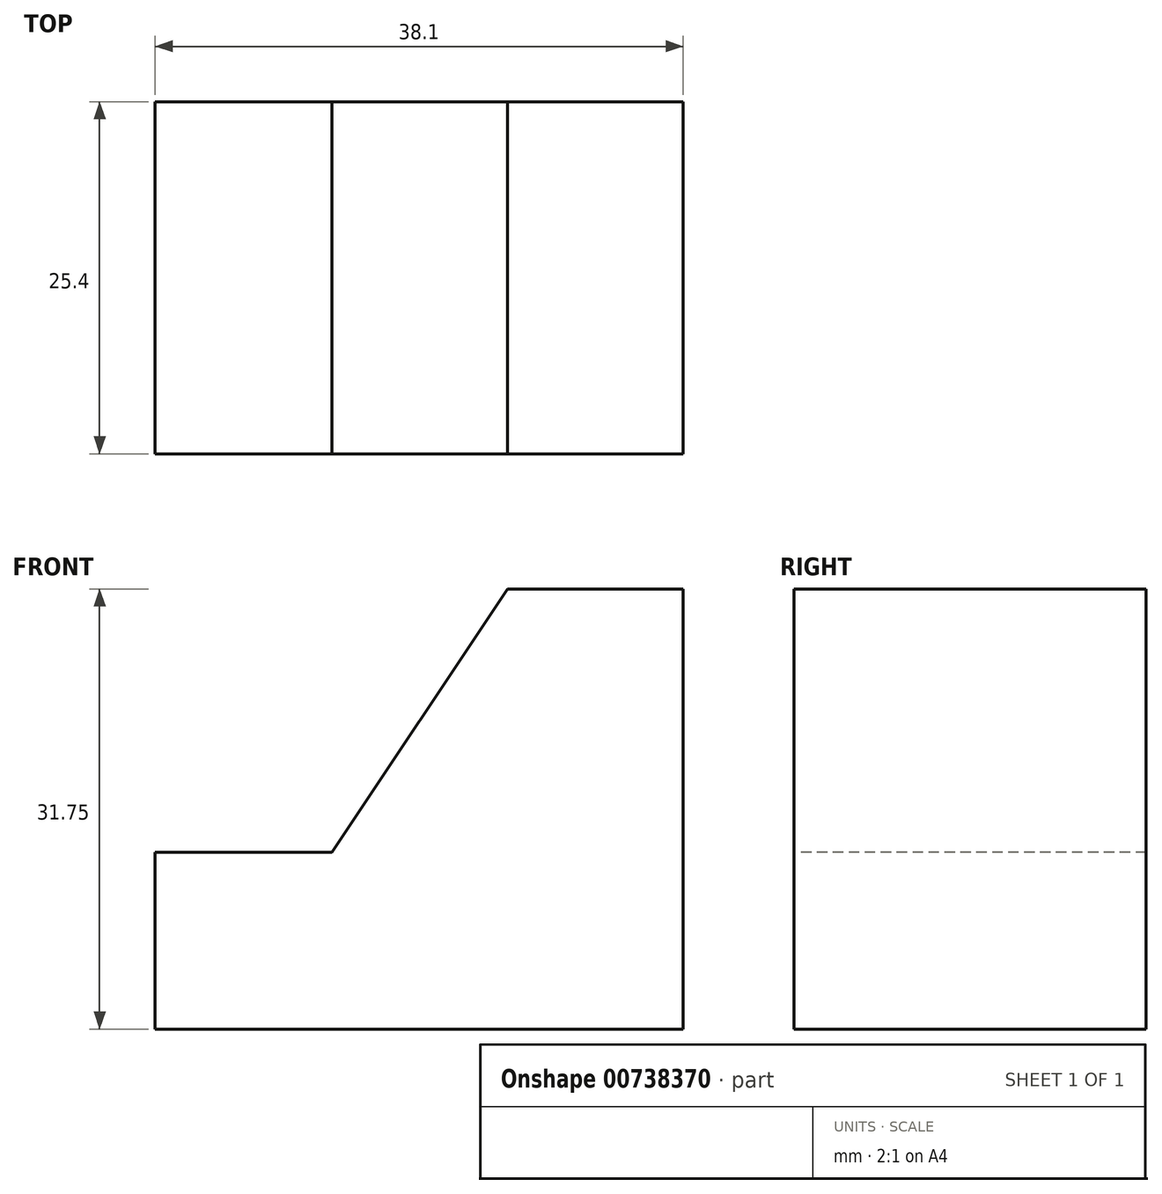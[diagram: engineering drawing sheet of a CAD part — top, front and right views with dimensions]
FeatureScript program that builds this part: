
annotation { "Feature Type Name" : "Feature", "Feature Type Description" : "" }
export const myFeature = defineFeature(function(context is Context, id is Id, definition is map)
    precondition{}
    {
        {
            var Q0;
            Q0=qCreatedBy(makeId("Front.planeOp"),FACE);
            var sketch = newSketch(context, id + "F0", { "sketchPlane" : qUnion([Q0])});
            skLineSegment(sketch, "E0", {"start": v(0, 0) * mm, "end": v(0, 31.75) * mm});
            skLineSegment(sketch, "E1", {"start": v(0, 31.75) * mm, "end": v(38.1, 31.75) * mm});
            skLineSegment(sketch, "E2", {"start": v(38.1, 31.75) * mm, "end": v(38.1, 0) * mm});
            skLineSegment(sketch, "E3", {"start": v(38.1, 0) * mm, "end": v(0, 0) * mm});
            skSolve(sketch);
        }
        {
            var Q0;
            Q0=makeQuery(id+"F0.imprint","IMPRINT",FACE,{"disambiguationData":[TD([[makeQuery(id+"F0.imprint","IMPRINT",EDGE,{"derivedFrom":sQuery(id+"F0.wireOp",EDGE,"E0")}),-1.0]])]});
            extrude(context, id + "F1", {"entities" : qUnion([Q0]), "depth" : 25.4 * mm, "offsetDistance" : 25.4 * mm});
        }
        {
            var Q0;
            Q0=qCreatedBy(makeId("Front.planeOp"),FACE);
            var sketch = newSketch(context, id + "F2", { "sketchPlane" : qUnion([Q0])});
            skLineSegment(sketch, "E4", {"start": v(23.02, 31.26) * mm, "end": v(23.02, 8.34) * mm});
            skLineSegment(sketch, "E5", {"start": v(23.02, 8.34) * mm, "end": v(0, 8.34) * mm});
            skLineSegment(sketch, "E6", {"start": v(0, 8.34) * mm, "end": v(0, 12.56) * mm});
            skLineSegment(sketch, "E7", {"start": v(0, 12.56) * mm, "end": v(23.02, 31.26) * mm});
            skSolve(sketch);
        }
        {
            var Q0;
            Q0=makeQuery(id+"F2.imprint","IMPRINT",FACE,{"disambiguationData":[TD([[makeQuery(id+"F2.imprint","IMPRINT",EDGE,{"derivedFrom":sQuery(id+"F2.wireOp",EDGE,"E4")}),-1.0]])]});
            extrude(context, id + "F3", {"entities" : qUnion([Q0]), "operationType" : NewBodyOperationType.REMOVE, "oppositeDirection" : true, "depth" : 25.4 * mm, "offsetDistance" : 25.4 * mm});
        }
        {
            var Q0;
            Q0=makeQuery(id+"F1.opExtrude","CAP_FACE",FACE,{"disambiguationData":[OSD([sQuery(id+"F0.wireOp",EDGE,"E0"),sQuery(id+"F0.wireOp",EDGE,"E1"),sQuery(id+"F0.wireOp",EDGE,"E2"),sQuery(id+"F0.wireOp",EDGE,"E3")])],"isStart":false});
            var sketch = newSketch(context, id + "F4", { "sketchPlane" : qUnion([Q0])});
            skLineSegment(sketch, "E8", {"start": v(0, 0) * mm, "end": v(0, 12.77) * mm});
            skLineSegment(sketch, "E9", {"start": v(0, 12.77) * mm, "end": v(12.77, 12.77) * mm});
            skLineSegment(sketch, "E10", {"start": v(38.1, 31.75) * mm, "end": v(25.43, 31.75) * mm});
            skLineSegment(sketch, "E11", {"start": v(0, 8.54) * mm, "end": v(0, 10.15) * mm});
            skLineSegment(sketch, "E12", {"start": v(25.43, 31.75) * mm, "end": v(12.77, 12.77) * mm});
            skSolve(sketch);
        }
        {
            var Q0;
            {var subQ0=sQuery(id+"F4.wireOp",EDGE,"E9");Q0=makeQuery(id+"F4.imprint","IMPRINT",FACE,{"disambiguationData":[TD([[makeQuery(id+"F4.imprint","IMPRINT",EDGE,{"derivedFrom":subQ0}),1.0]])]});}
            extrude(context, id + "F5", {"entities" : qUnion([Q0]), "operationType" : NewBodyOperationType.REMOVE, "endBound" : BoundingType.THROUGH_ALL, "oppositeDirection" : true, "depth" : 25.4 * mm, "offsetDistance" : 25.4 * mm});
        }
    });
